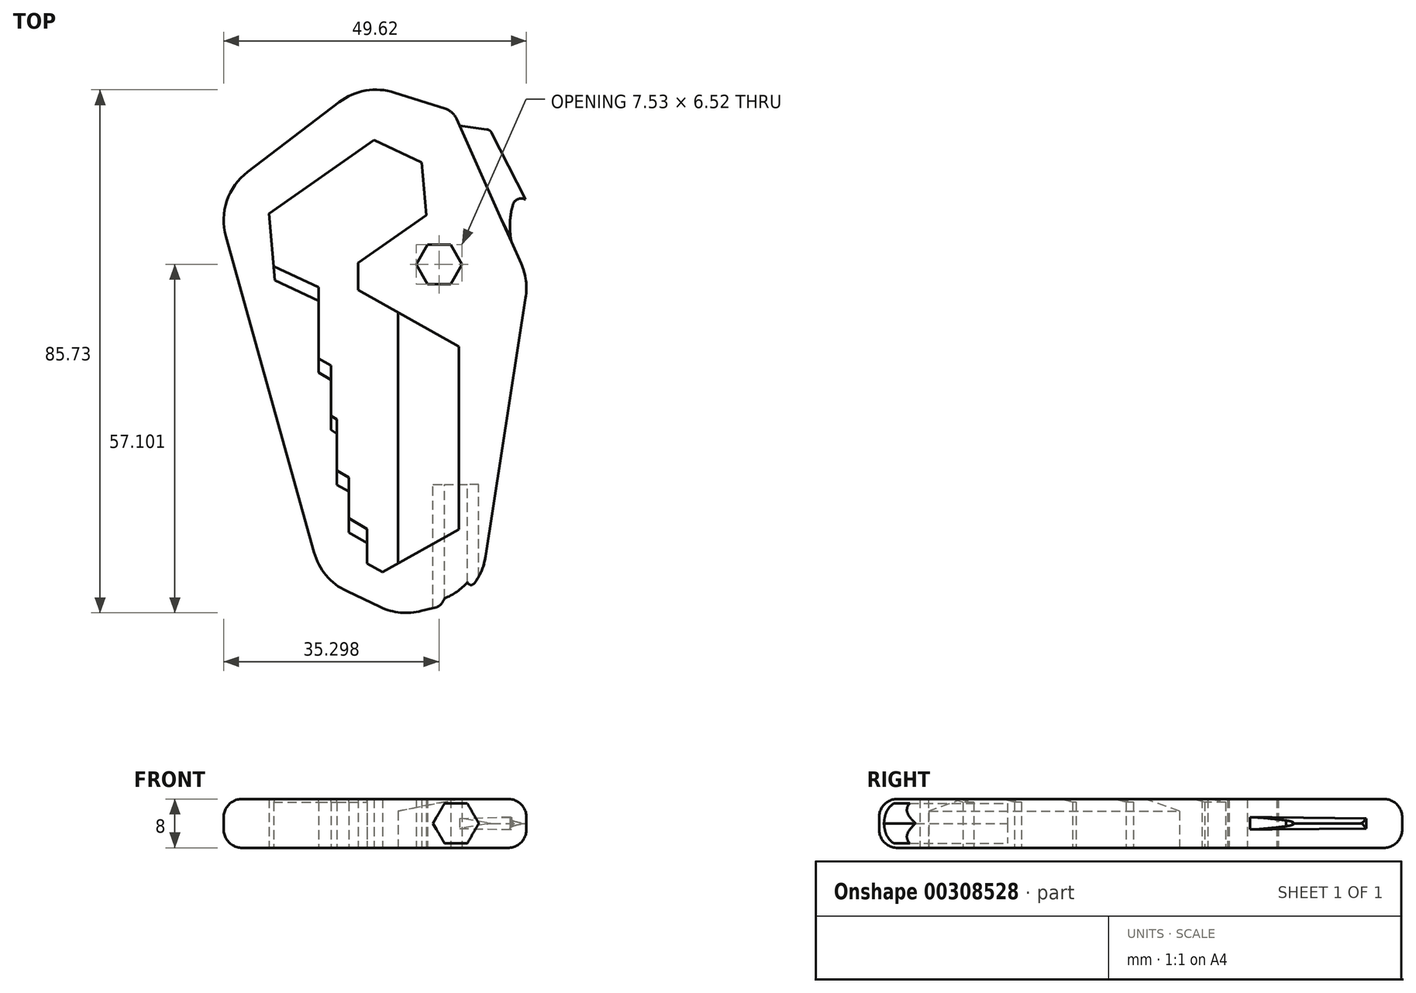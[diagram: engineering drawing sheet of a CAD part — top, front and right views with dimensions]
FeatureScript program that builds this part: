
annotation { "Feature Type Name" : "Feature", "Feature Type Description" : "" }
export const myFeature = defineFeature(function(context is Context, id is Id, definition is map)
    precondition{}
    {
        {
            var Q0;
            Q0=qCreatedBy(makeId("Top.planeOp"),FACE);
            var sketch = newSketch(context, id + "F0", { "sketchPlane" : qUnion([Q0])});
            skLineSegment(sketch, "E0.3", {"start": v(-5.5, -3.18) * mm, "end": v(-5.5, 5.06) * mm});
            skLineSegment(sketch, "E1", {"start": v(5.5, 13.8) * mm, "end": v(-1.02, 17.48) * mm});
            skLineSegment(sketch, "E2", {"start": v(-1.02, 17.48) * mm, "end": v(-1.02, 21.92) * mm});
            skLineSegment(sketch, "E3.0", {"start": v(9.4, 38.37) * mm, "end": v(10.15, 29.74) * mm});
            skLineSegment(sketch, "E3.1", {"start": v(10.15, 29.74) * mm, "end": v(-1.02, 21.92) * mm});
            skLineSegment(sketch, "E3.2", {"start": v(-7.52, 17.92) * mm, "end": v(-14.9, 21.36) * mm});
            skLineSegment(sketch, "E3.3", {"start": v(-14.9, 21.36) * mm, "end": v(-15.65, 29.99) * mm});
            skLineSegment(sketch, "E3.4", {"start": v(-15.65, 29.99) * mm, "end": v(1.55, 42.03) * mm});
            skLineSegment(sketch, "E3.5", {"start": v(1.55, 42.03) * mm, "end": v(9.4, 38.37) * mm});
            skPoint(sketch, "E3.0.midPoint", {"position": v(9.78, 34.06) * mm});
            skLineSegment(sketch, "E4", {"start": v(12.46, -34.35) * mm, "end": v(9.35, -35.14) * mm});
            skLineSegment(sketch, "E5", {"start": v(2.6, -34.5) * mm, "end": v(-2.9, -31.9) * mm});
            skLineSegment(sketch, "E6", {"start": v(-8.25, -25.54) * mm, "end": v(-22.69, 26.19) * mm});
            skLineSegment(sketch, "E7", {"start": v(-19.12, 36.83) * mm, "end": v(-4.14, 48.24) * mm});
            skLineSegment(sketch, "E8", {"start": v(4.96, 49.81) * mm, "end": v(14.56, 46.75) * mm});
            skLineSegment(sketch, "E9", {"start": v(14.56, 46.75) * mm, "end": v(25.7, 21.77) * mm});
            skLineSegment(sketch, "E10", {"start": v(26.44, 16.16) * mm, "end": v(19.87, -26.19) * mm});
            skLineSegment(sketch, "E11.2", {"start": v(0.45, -21.7) * mm, "end": v(-2.57, -19.96) * mm});
            skLineSegment(sketch, "E11.3", {"start": v(-2.57, -19.96) * mm, "end": v(-2.57, -13.21) * mm});
            skLineSegment(sketch, "E12.1", {"start": v(5.52, -27.3) * mm, "end": v(2.95, -28.73) * mm});
            skLineSegment(sketch, "E12.3", {"start": v(0.45, -27.36) * mm, "end": v(0.45, -21.7) * mm});
            skLineSegment(sketch, "E13.2", {"start": v(-2.57, -13.27) * mm, "end": v(-4.5, -12.15) * mm});
            skLineSegment(sketch, "E13.3", {"start": v(-4.5, -12.15) * mm, "end": v(-4.5, -3.75) * mm});
            skLineSegment(sketch, "E14.2", {"start": v(-5.5, 5.06) * mm, "end": v(-7.52, 6.22) * mm});
            skLineSegment(sketch, "E14.3", {"start": v(-7.52, 6.22) * mm, "end": v(-7.52, 17.92) * mm});
            skPoint(sketch, "E15.orphan", {"position": v(-1.02, 21.36) * mm});
            skLineSegment(sketch, "E16.trimOffspring", {"start": v(-4.5, -3.75) * mm, "end": v(-5.5, -3.18) * mm});
            skPoint(sketch, "E17.orphan", {"position": v(-4.5, -6.38) * mm});
            skPoint(sketch, "E18.orphan", {"position": v(-5.5, 3.18) * mm});
            skPoint(sketch, "E19.orphan", {"position": v(-2.57, -15.34) * mm});
            skPoint(sketch, "E12.4.start.orphan", {"position": v(0.45, -23.26) * mm});
            skLineSegment(sketch, "E20.0", {"start": v(2.95, -28.73) * mm, "end": v(0.45, -27.36) * mm});
            skLineSegment(sketch, "E21", {"start": v(5.5, 13.8) * mm, "end": v(5.52, -27.3) * mm});
            skPoint(sketch, "E22.visualSharp", {"position": v(-24.51, 32.72) * mm});
            skArc(sketch, "E22.filletArc", {"start": v(-19.12, 36.83) * mm, "mid": v(-22.54, 32.05) * mm, "end": v(-22.69, 26.19) * mm});
            skPoint(sketch, "E23.visualSharp", {"position": v(0, 51.4) * mm});
            skArc(sketch, "E23.filletArc", {"start": v(4.96, 49.81) * mm, "mid": v(0.22, 50.14) * mm, "end": v(-4.14, 48.24) * mm});
            skPoint(sketch, "E24.visualSharp", {"position": v(26.9, 19.08) * mm});
            skArc(sketch, "E24.filletArc", {"start": v(26.44, 16.16) * mm, "mid": v(26.47, 19.02) * mm, "end": v(25.7, 21.77) * mm});
            skPoint(sketch, "E25.visualSharp", {"position": v(18.86, -32.71) * mm});
            skArc(sketch, "E25.filletArc", {"start": v(12.46, -34.35) * mm, "mid": v(17.4, -31.38) * mm, "end": v(19.87, -26.19) * mm});
            skPoint(sketch, "E26.visualSharp", {"position": v(5.86, -36.03) * mm});
            skArc(sketch, "E26.filletArc", {"start": v(2.6, -34.5) * mm, "mid": v(5.92, -35.4) * mm, "end": v(9.35, -35.14) * mm});
            skPoint(sketch, "E27.visualSharp", {"position": v(-7.03, -29.94) * mm});
            skArc(sketch, "E27.filletArc", {"start": v(-8.25, -25.54) * mm, "mid": v(-6.27, -29.3) * mm, "end": v(-2.9, -31.9) * mm});
            skCircle(sketch, "E28.cCircle", {"center": v(12.24, 21.65) * mm, "radius": 3.26 * mm, "construction": true});
            skLineSegment(sketch, "E28.0", {"start": v(10.35, 24.91) * mm, "end": v(14.12, 24.91) * mm});
            skLineSegment(sketch, "E28.1", {"start": v(14.12, 24.91) * mm, "end": v(16, 21.65) * mm});
            skLineSegment(sketch, "E28.2", {"start": v(16, 21.65) * mm, "end": v(14.12, 18.39) * mm});
            skLineSegment(sketch, "E28.3", {"start": v(14.12, 18.39) * mm, "end": v(10.35, 18.39) * mm});
            skLineSegment(sketch, "E28.4", {"start": v(10.35, 18.39) * mm, "end": v(8.47, 21.65) * mm});
            skLineSegment(sketch, "E28.5", {"start": v(8.47, 21.65) * mm, "end": v(10.35, 24.91) * mm});
            skPoint(sketch, "E28.0.midPoint", {"position": v(12.24, 24.91) * mm});
            skArc(sketch, "E29", {"start": v(24.28, 31.26) * mm, "mid": v(23.86, 28.3) * mm, "end": v(24.1, 25.32) * mm});
            skArc(sketch, "E30", {"start": v(26.4, 32.3) * mm, "mid": v(25.08, 32.33) * mm, "end": v(24.28, 31.26) * mm});
            skLineSegment(sketch, "E31", {"start": v(20.84, 43.24) * mm, "end": v(26.4, 32.3) * mm});
            skLineSegment(sketch, "E32", {"start": v(20.09, 43.78) * mm, "end": v(15.6, 44.4) * mm});
            skPoint(sketch, "E33.visualSharp", {"position": v(20.6, 43.7) * mm});
            skArc(sketch, "E33.filletArc", {"start": v(20.84, 43.24) * mm, "mid": v(20.53, 43.6) * mm, "end": v(20.09, 43.78) * mm});
            skSolve(sketch);
        }
        {
            var Q0;
            Q0=makeQuery(id+"F0.imprint","IMPRINT",FACE,{"disambiguationData":[TD([[makeQuery(id+"F0.imprint","IMPRINT",EDGE,{"derivedFrom":sQuery(id+"F0.wireOp",EDGE,"E0.3")}),1.0]])]});
            extrude(context, id + "F1", {"entities" : qUnion([Q0]), "depth" : 8 * mm});
        }
        {
            var Q0;
            Q0=qCreatedBy(makeId("Front.planeOp"),FACE);
            var sketch = newSketch(context, id + "F2", { "sketchPlane" : qUnion([Q0])});
            skCircle(sketch, "E34.cCircle", {"center": v(15, 4) * mm, "radius": 3.25 * mm, "construction": true});
            skLineSegment(sketch, "E34.0", {"start": v(13.12, 7.25) * mm, "end": v(16.88, 7.25) * mm});
            skLineSegment(sketch, "E34.1", {"start": v(16.88, 7.25) * mm, "end": v(18.75, 4) * mm});
            skLineSegment(sketch, "E34.2", {"start": v(18.75, 4) * mm, "end": v(16.88, 0.75) * mm});
            skLineSegment(sketch, "E34.3", {"start": v(16.88, 0.75) * mm, "end": v(13.12, 0.75) * mm});
            skLineSegment(sketch, "E34.4", {"start": v(13.12, 0.75) * mm, "end": v(11.25, 4) * mm});
            skLineSegment(sketch, "E34.5", {"start": v(11.25, 4) * mm, "end": v(13.12, 7.25) * mm});
            skPoint(sketch, "E34.0.midPoint", {"position": v(15, 7.25) * mm});
            skSolve(sketch);
        }
        {
            var Q0;
            Q0=makeQuery(id+"F2.imprint","IMPRINT",FACE,{"disambiguationData":[TD([[makeQuery(id+"F2.imprint","IMPRINT",EDGE,{"derivedFrom":sQuery(id+"F2.wireOp",EDGE,"E34.0")}),-1.0]])]});
            extrude(context, id + "F3", {"entities" : qUnion([Q0]), "operationType" : NewBodyOperationType.REMOVE, "depth" : 46.4 * mm, "hasSecondDirection" : true, "secondDirectionOppositeDirection" : false, "secondDirectionDepth" : 14.4 * mm});
        }
        {
            var Q0;
            Q0=makeQuery(id+"F1.opExtrude","CAP_EDGE",EDGE,{"disambiguationData":[OSD([sQuery(id+"F0.wireOp",EDGE,"E6")])],"isStart":false});
            var Q1;
            Q1=makeQuery(id+"F1.opExtrude","CAP_EDGE",EDGE,{"disambiguationData":[OSD([sQuery(id+"F0.wireOp",EDGE,"E10")])],"isStart":true});
            var Q2;
            Q2=makeQuery(id+"F1.opExtrude","SWEPT_EDGE",EDGE,{"disambiguationData":[OSD([sQuery(id+"F0.wireOp",EDGE,"E8"),sQuery(id+"F0.wireOp",EDGE,"E9"),sQuery(id+"F0.wireOp",EDGE,"lwQlDwhy-GB8o-fgLY-QJiR-cFOKYwZACIO8")])]});
            fillet(context, id + "F4", {"entities" : qUnion([Q0, Q1, Q2]), "radius" : 3 * mm, "tangentPropagation" : true, "allowEdgeOverflow" : false});
        }
        {
            var Q0;
            Q0=makeQuery(id+"F1.opExtrude","CAP_EDGE",EDGE,{"disambiguationData":[OSD([sQuery(id+"F0.wireOp",EDGE,"E21")])],"isStart":false});
            var Q1;
            {var subQ0=sQuery(id+"F0.wireOp",EDGE,"E6");Q1=makeQuery(id+"F4.opFillet","BLEND_EDGE",EDGE,{"blendedFrom":[makeQuery(id+"F1.opExtrude","CAP_EDGE",EDGE,{"disambiguationData":[OSD([subQ0])],"isStart":false}),makeQuery(id+"F1.opExtrude","CAP_FACE",FACE,{"disambiguationData":[OSD([sQuery(id+"F0.wireOp",EDGE,"E0.3"),sQuery(id+"F0.wireOp",EDGE,"E1"),sQuery(id+"F0.wireOp",EDGE,"E2"),sQuery(id+"F0.wireOp",EDGE,"E3.0"),sQuery(id+"F0.wireOp",EDGE,"E3.1"),sQuery(id+"F0.wireOp",EDGE,"E3.2"),sQuery(id+"F0.wireOp",EDGE,"E3.3"),sQuery(id+"F0.wireOp",EDGE,"E3.4"),sQuery(id+"F0.wireOp",EDGE,"E3.5"),sQuery(id+"F0.wireOp",EDGE,"E4"),sQuery(id+"F0.wireOp",EDGE,"E5"),subQ0,sQuery(id+"F0.wireOp",EDGE,"E7"),sQuery(id+"F0.wireOp",EDGE,"E8"),sQuery(id+"F0.wireOp",EDGE,"E9"),sQuery(id+"F0.wireOp",EDGE,"E10"),sQuery(id+"F0.wireOp",EDGE,"E11.2"),sQuery(id+"F0.wireOp",EDGE,"E11.3"),sQuery(id+"F0.wireOp",EDGE,"E12.1"),sQuery(id+"F0.wireOp",EDGE,"E12.3"),sQuery(id+"F0.wireOp",EDGE,"E13.2"),sQuery(id+"F0.wireOp",EDGE,"E13.3"),sQuery(id+"F0.wireOp",EDGE,"E14.2"),sQuery(id+"F0.wireOp",EDGE,"E14.3"),sQuery(id+"F0.wireOp",EDGE,"E16.trimOffspring"),sQuery(id+"F0.wireOp",EDGE,"E20.0"),sQuery(id+"F0.wireOp",EDGE,"E21"),sQuery(id+"F0.wireOp",EDGE,"E22.filletArc"),sQuery(id+"F0.wireOp",EDGE,"E23.filletArc"),sQuery(id+"F0.wireOp",EDGE,"E24.filletArc"),sQuery(id+"F0.wireOp",EDGE,"E25.filletArc"),sQuery(id+"F0.wireOp",EDGE,"E26.filletArc"),sQuery(id+"F0.wireOp",EDGE,"E27.filletArc"),sQuery(id+"F0.wireOp",EDGE,"E28.0"),sQuery(id+"F0.wireOp",EDGE,"E28.1"),sQuery(id+"F0.wireOp",EDGE,"E28.2"),sQuery(id+"F0.wireOp",EDGE,"E28.3"),sQuery(id+"F0.wireOp",EDGE,"E28.4"),sQuery(id+"F0.wireOp",EDGE,"E28.5")])],"isStart":false})],"blendedInto":[makeQuery(id+"F1.opExtrude","CAP_FACE",FACE,{"disambiguationData":[OSD([sQuery(id+"F0.wireOp",EDGE,"E0.3"),sQuery(id+"F0.wireOp",EDGE,"E1"),sQuery(id+"F0.wireOp",EDGE,"E2"),sQuery(id+"F0.wireOp",EDGE,"E3.0"),sQuery(id+"F0.wireOp",EDGE,"E3.1"),sQuery(id+"F0.wireOp",EDGE,"E3.2"),sQuery(id+"F0.wireOp",EDGE,"E3.3"),sQuery(id+"F0.wireOp",EDGE,"E3.4"),sQuery(id+"F0.wireOp",EDGE,"E3.5"),sQuery(id+"F0.wireOp",EDGE,"E4"),sQuery(id+"F0.wireOp",EDGE,"E5"),subQ0,sQuery(id+"F0.wireOp",EDGE,"E7"),sQuery(id+"F0.wireOp",EDGE,"E8"),sQuery(id+"F0.wireOp",EDGE,"E9"),sQuery(id+"F0.wireOp",EDGE,"E10"),sQuery(id+"F0.wireOp",EDGE,"E11.2"),sQuery(id+"F0.wireOp",EDGE,"E11.3"),sQuery(id+"F0.wireOp",EDGE,"E12.1"),sQuery(id+"F0.wireOp",EDGE,"E12.3"),sQuery(id+"F0.wireOp",EDGE,"E13.2"),sQuery(id+"F0.wireOp",EDGE,"E13.3"),sQuery(id+"F0.wireOp",EDGE,"E14.2"),sQuery(id+"F0.wireOp",EDGE,"E14.3"),sQuery(id+"F0.wireOp",EDGE,"E16.trimOffspring"),sQuery(id+"F0.wireOp",EDGE,"E20.0"),sQuery(id+"F0.wireOp",EDGE,"E21"),sQuery(id+"F0.wireOp",EDGE,"E22.filletArc"),sQuery(id+"F0.wireOp",EDGE,"E23.filletArc"),sQuery(id+"F0.wireOp",EDGE,"E24.filletArc"),sQuery(id+"F0.wireOp",EDGE,"E25.filletArc"),sQuery(id+"F0.wireOp",EDGE,"E26.filletArc"),sQuery(id+"F0.wireOp",EDGE,"E27.filletArc"),sQuery(id+"F0.wireOp",EDGE,"E28.0"),sQuery(id+"F0.wireOp",EDGE,"E28.1"),sQuery(id+"F0.wireOp",EDGE,"E28.2"),sQuery(id+"F0.wireOp",EDGE,"E28.3"),sQuery(id+"F0.wireOp",EDGE,"E28.4"),sQuery(id+"F0.wireOp",EDGE,"E28.5")])],"isStart":false})]});}
            chamfer(context, id + "F5", {"entities" : qUnion([Q0, Q1]), "chamferType" : ChamferType.TWO_OFFSETS, "width1" : 10 * mm, "oppositeDirection" : false, "width2" : 2 * mm, "tangentPropagation" : true});
        }
        {
            var Q0;
            Q0=makeQuery(id+"F1.opExtrude","CAP_EDGE",EDGE,{"disambiguationData":[OSD([sQuery(id+"F0.wireOp",EDGE,"E13.2")])],"isStart":false});
            var Q1;
            Q1=makeQuery(id+"F1.opExtrude","CAP_EDGE",EDGE,{"disambiguationData":[OSD([sQuery(id+"F0.wireOp",EDGE,"E11.2")])],"isStart":false});
            var Q2;
            Q2=makeQuery(id+"F1.opExtrude","CAP_EDGE",EDGE,{"disambiguationData":[OSD([sQuery(id+"F0.wireOp",EDGE,"E16.trimOffspring")])],"isStart":false});
            var Q3;
            Q3=makeQuery(id+"F1.opExtrude","CAP_EDGE",EDGE,{"disambiguationData":[OSD([sQuery(id+"F0.wireOp",EDGE,"E14.2")])],"isStart":false});
            var Q4;
            Q4=makeQuery(id+"F1.opExtrude","CAP_EDGE",EDGE,{"disambiguationData":[OSD([sQuery(id+"F0.wireOp",EDGE,"E3.2")])],"isStart":false});
            chamfer(context, id + "F6", {"entities" : qUnion([Q0, Q1, Q2, Q3, Q4]), "chamferType" : ChamferType.TWO_OFFSETS, "width1" : 2 * mm, "oppositeDirection" : false, "width2" : 0.5 * mm, "tangentPropagation" : true});
        }
        {
            var Q0;
            {var subQ1=sQuery(id+"F0.wireOp",EDGE,"E29");Q0=makeQuery(id+"F0.imprint","IMPRINT",FACE,{"disambiguationData":[TD([[makeQuery(id+"F0.imprint","IMPRINT",EDGE,{"derivedFrom":subQ1}),-1.0]])]});}
            extrude(context, id + "F7", {"entities" : qUnion([Q0]), "operationType" : NewBodyOperationType.ADD, "depth" : 5 * mm, "hasSecondDirection" : true, "secondDirectionOppositeDirection" : false, "secondDirectionDepth" : 3 * mm});
        }
        {
            var Q0;
            Q0=makeQuery(id+"F7.opExtrude","CAP_EDGE",EDGE,{"disambiguationData":[OSD([sQuery(id+"F0.wireOp",EDGE,"E31")])],"isStart":false});
            var Q1;
            Q1=makeQuery(id+"F7.opExtrude","CAP_EDGE",EDGE,{"disambiguationData":[OSD([sQuery(id+"F0.wireOp",EDGE,"E31")])],"isStart":true});
            chamfer(context, id + "F8", {"entities" : qUnion([Q0, Q1]), "chamferType" : ChamferType.TWO_OFFSETS, "width1" : 1 * mm, "oppositeDirection" : false, "width2" : 5 * mm, "tangentPropagation" : true});
        }
    });
